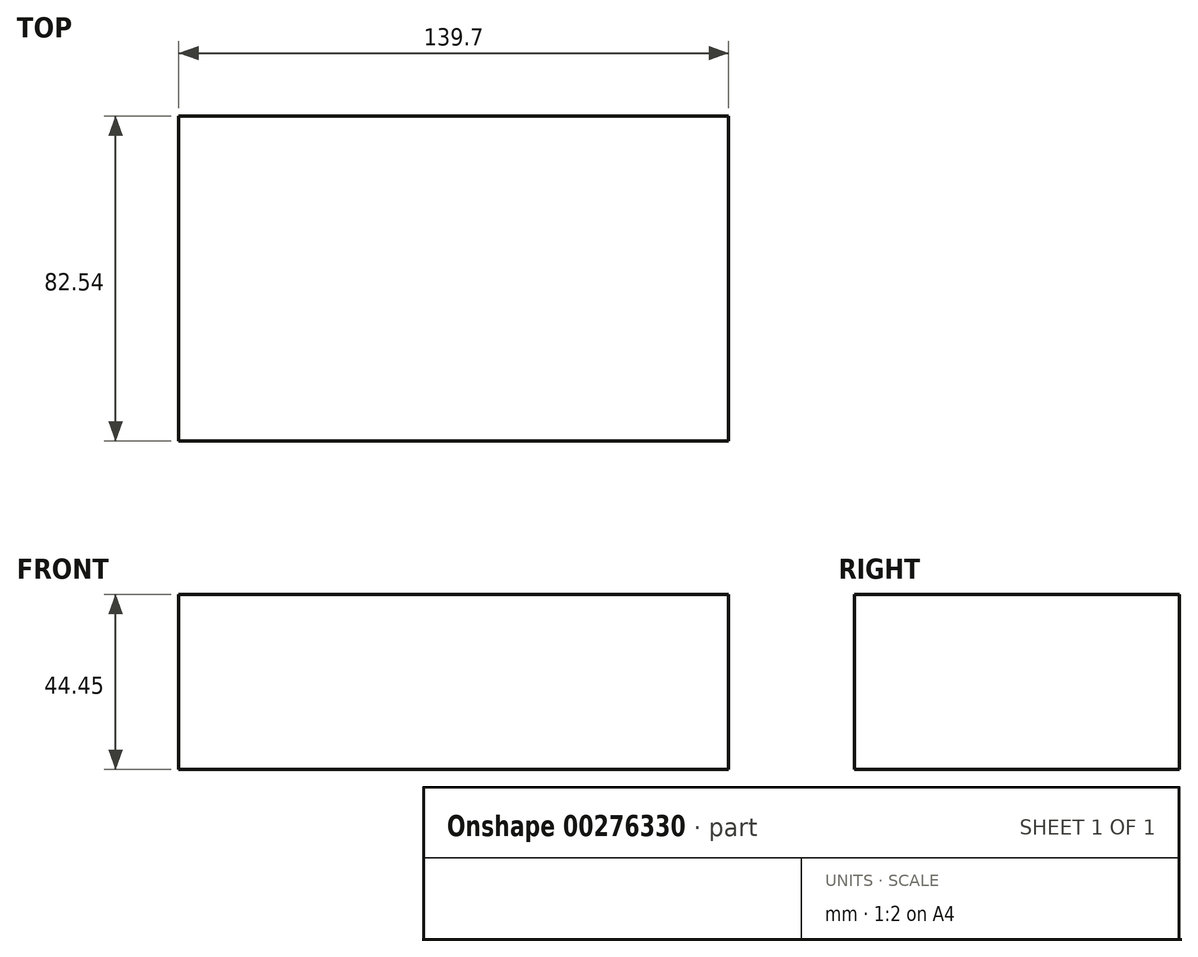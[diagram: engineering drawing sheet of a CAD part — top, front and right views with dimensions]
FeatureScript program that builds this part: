
annotation { "Feature Type Name" : "Feature", "Feature Type Description" : "" }
export const myFeature = defineFeature(function(context is Context, id is Id, definition is map)
    precondition{}
    {
        {
            var Q0;
            Q0=qCreatedBy(makeId("Top.planeOp"),FACE);
            var sketch = newSketch(context, id + "F0", { "sketchPlane" : qUnion([Q0])});
            skLineSegment(sketch, "E0.bottom", {"start": v(69.85, -41.28) * mm, "end": v(-69.85, -41.28) * mm});
            skLineSegment(sketch, "E0.top", {"start": v(69.85, 41.28) * mm, "end": v(-69.85, 41.27) * mm});
            skLineSegment(sketch, "E0.left", {"start": v(69.85, -41.28) * mm, "end": v(69.85, 41.28) * mm});
            skLineSegment(sketch, "E0.right", {"start": v(-69.85, -41.28) * mm, "end": v(-69.85, 41.27) * mm});
            skPoint(sketch, "E0.middle", {"position": v(0, 0) * mm});
            skSolve(sketch);
        }
        {
            var Q0;
            Q0=makeQuery(id+"F0.imprint","IMPRINT",FACE,{"disambiguationData":[TD([[makeQuery(id+"F0.imprint","IMPRINT",EDGE,{"derivedFrom":sQuery(id+"F0.wireOp",EDGE,"E0.bottom")}),-1.0]])]});
            extrude(context, id + "F1", {"entities" : qUnion([Q0]), "depth" : 44.45 * mm});
        }
    });
